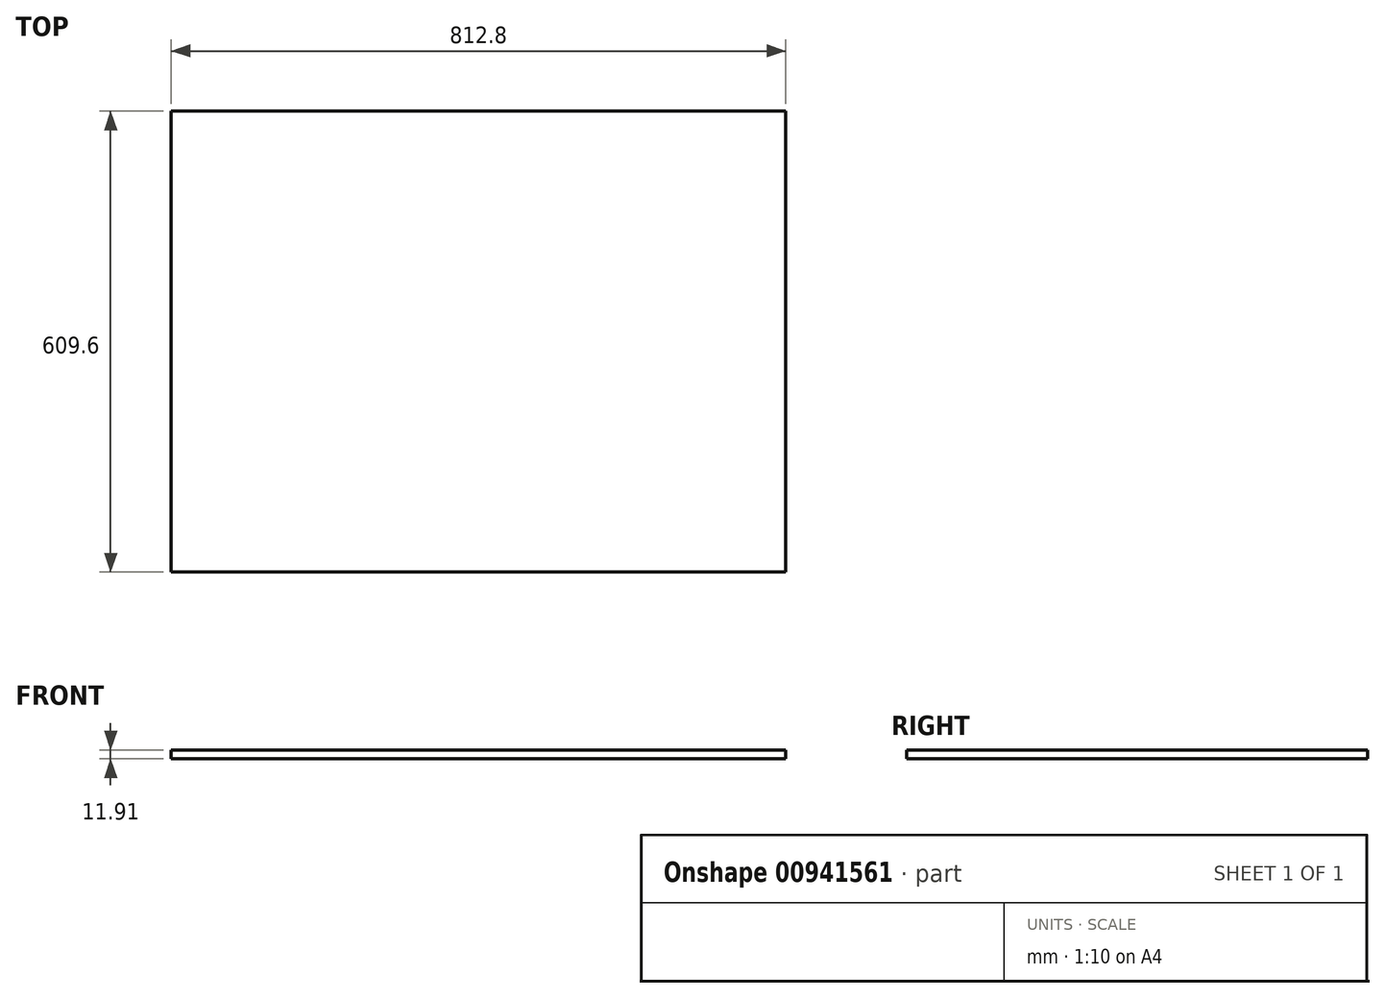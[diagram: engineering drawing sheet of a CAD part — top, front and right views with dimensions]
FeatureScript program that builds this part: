
annotation { "Feature Type Name" : "Feature", "Feature Type Description" : "" }
export const myFeature = defineFeature(function(context is Context, id is Id, definition is map)
    precondition{}
    {
        {
            var Q0;
            Q0=qCreatedBy(makeId("Top.planeOp"),FACE);
            var sketch = newSketch(context, id + "F0", { "sketchPlane" : qUnion([Q0])});
            skLineSegment(sketch, "E0.bottom", {"start": v(406.4, 304.8) * mm, "end": v(-406.4, 304.8) * mm});
            skLineSegment(sketch, "E0.top", {"start": v(406.4, -304.8) * mm, "end": v(-406.4, -304.8) * mm});
            skLineSegment(sketch, "E0.left", {"start": v(406.4, 304.8) * mm, "end": v(406.4, -304.8) * mm});
            skLineSegment(sketch, "E0.right", {"start": v(-406.4, 304.8) * mm, "end": v(-406.4, -304.8) * mm});
            skPoint(sketch, "E0.middle", {"position": v(0, 0) * mm});
            skSolve(sketch);
        }
        {
            var Q0;
            Q0 = qSketchRegion(id + "F0", true);
            extrude(context, id + "F1", {"entities" : qUnion([Q0]), "depth" : 11.9 * mm, "offsetDistance" : 25.4 * mm});
        }
    });
